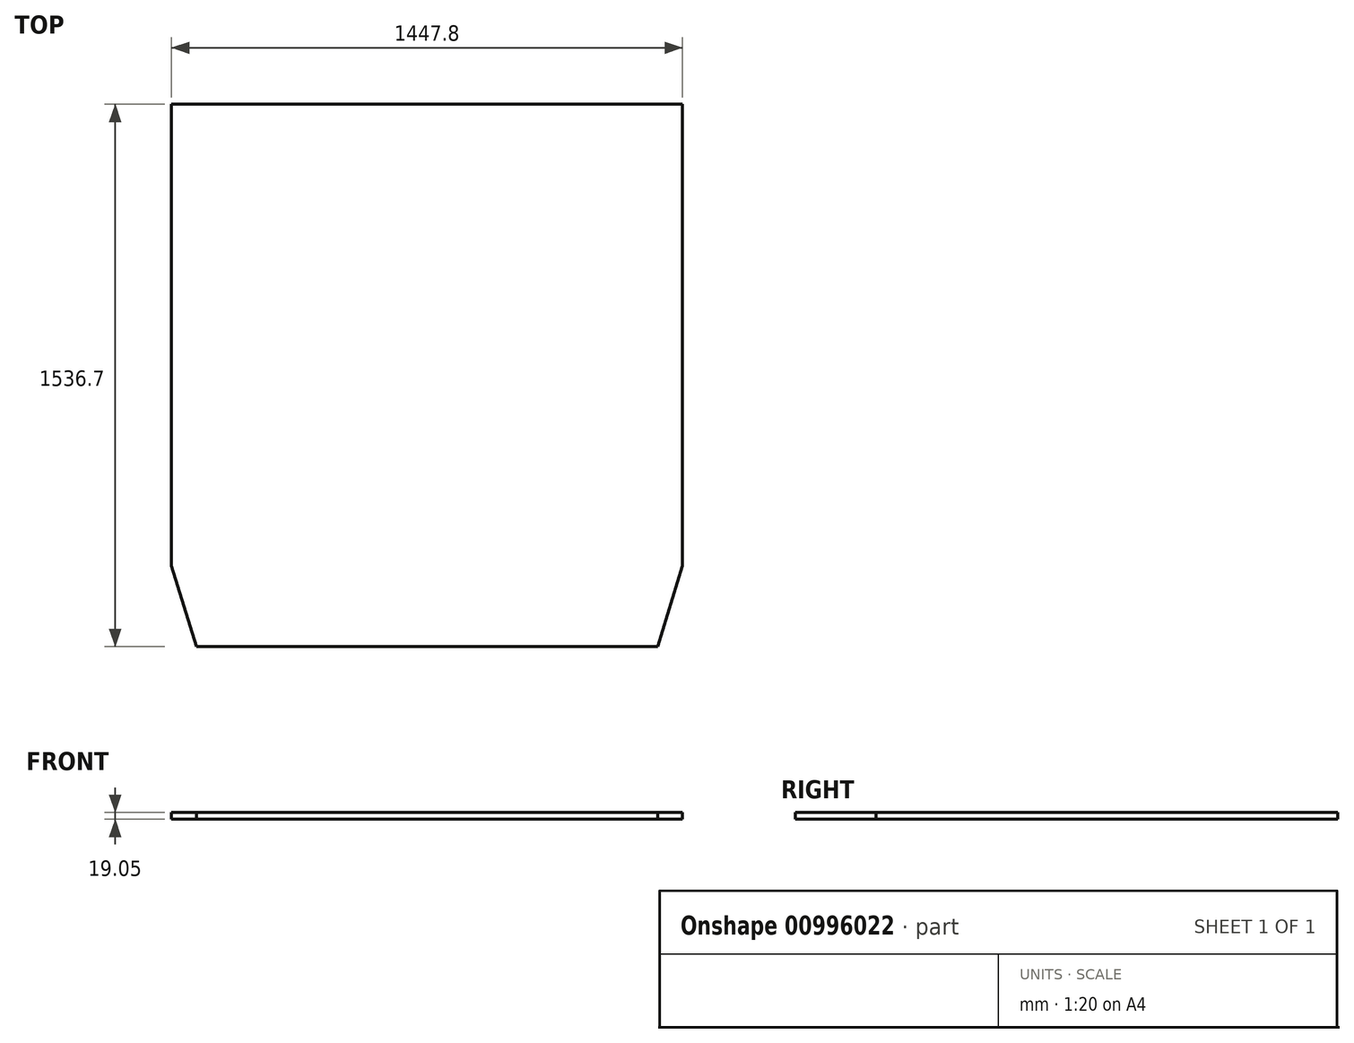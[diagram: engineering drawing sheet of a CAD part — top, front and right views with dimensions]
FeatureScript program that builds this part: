
annotation { "Feature Type Name" : "Feature", "Feature Type Description" : "" }
export const myFeature = defineFeature(function(context is Context, id is Id, definition is map)
    precondition{}
    {
        {
            var Q0;
            Q0=qCreatedBy(makeId("Top.planeOp"),FACE);
            var sketch = newSketch(context, id + "F0", { "sketchPlane" : qUnion([Q0])});
            skLineSegment(sketch, "E0.bottom", {"start": v(0, 0) * mm, "end": v(1447.8, 0) * mm});
            skLineSegment(sketch, "E0.top", {"start": v(0, 1536.7) * mm, "end": v(1447.8, 1536.7) * mm});
            skLineSegment(sketch, "E0.left", {"start": v(0, 0) * mm, "end": v(0, 1536.7) * mm});
            skLineSegment(sketch, "E0.right", {"start": v(1447.8, 0) * mm, "end": v(1447.8, 1536.7) * mm});
            skSolve(sketch);
        }
        {
            var Q0;
            Q0 = qSketchRegion(id + "F0", true);
            extrude(context, id + "F1", {"entities" : qUnion([Q0]), "depth" : 19.05 * mm, "offsetDistance" : 25.4 * mm});
        }
        {
            var Q0;
            Q0=makeQuery(id+"F1.opExtrude","SWEPT_EDGE",EDGE,{"disambiguationData":[OSD([sQuery(id+"F0.wireOp",EDGE,"E0.bottom"),sQuery(id+"F0.wireOp",EDGE,"E0.right")])]});
            var Q1;
            Q1=makeQuery(id+"F1.opExtrude","SWEPT_EDGE",EDGE,{"disambiguationData":[OSD([sQuery(id+"F0.wireOp",EDGE,"E0.bottom"),sQuery(id+"F0.wireOp",EDGE,"E0.left")])]});
            chamfer(context, id + "F2", {"entities" : qUnion([Q0, Q1]), "chamferType" : ChamferType.OFFSET_ANGLE, "width" : 228.6 * mm, "oppositeDirection" : false, "angle" : 17 * degree, "tangentPropagation" : true});
        }
    });
